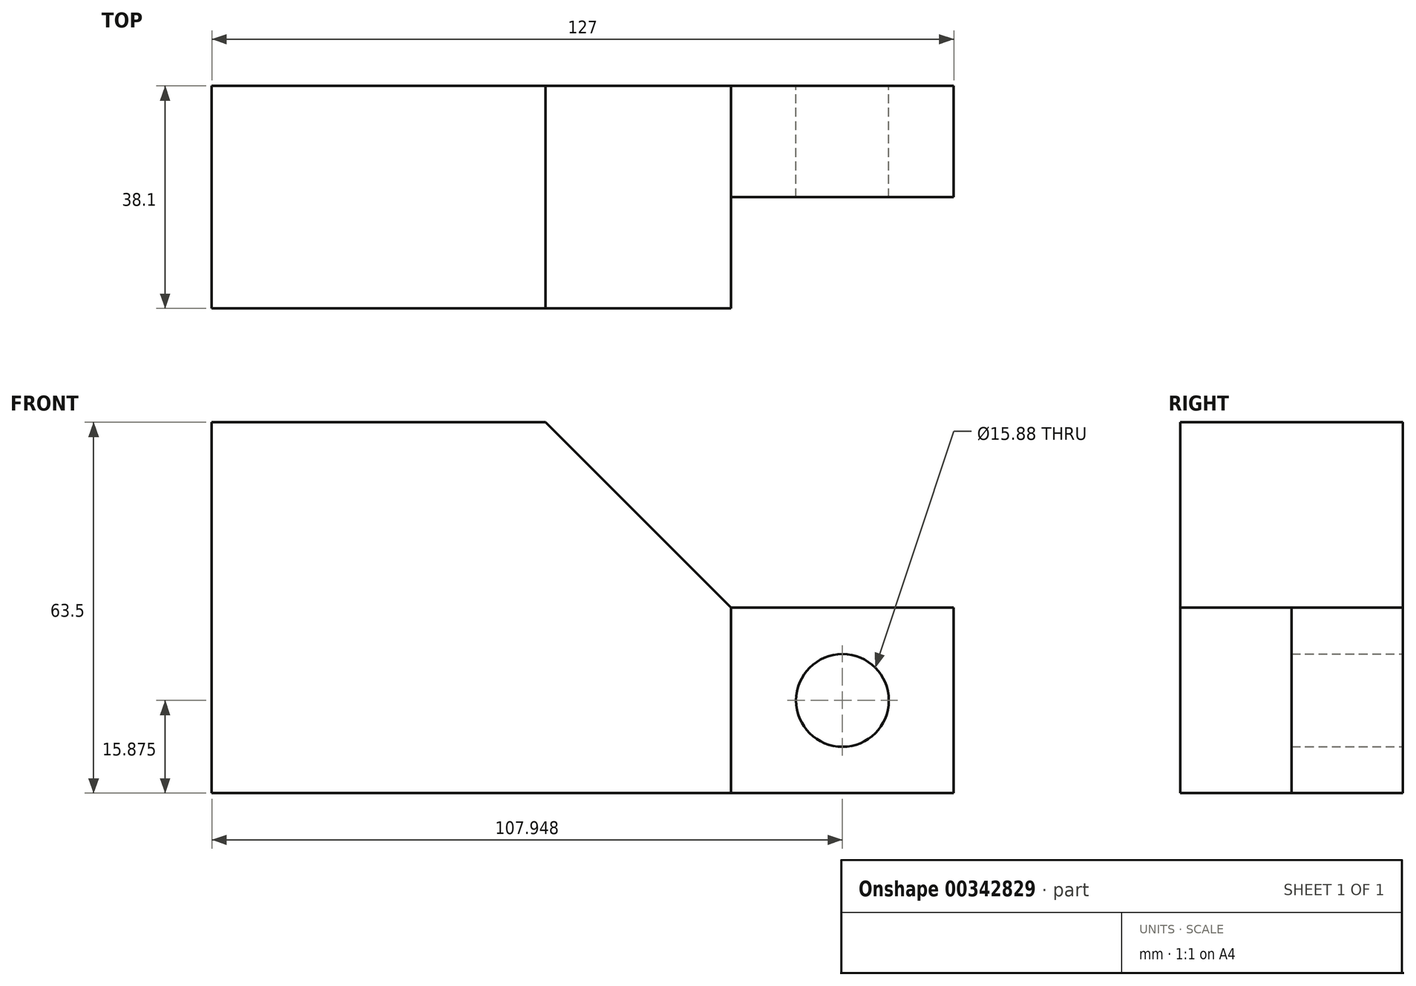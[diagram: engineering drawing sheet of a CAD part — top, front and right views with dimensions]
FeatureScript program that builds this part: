
annotation { "Feature Type Name" : "Feature", "Feature Type Description" : "" }
export const myFeature = defineFeature(function(context is Context, id is Id, definition is map)
    precondition{}
    {
        {
            var Q0;
            Q0=qCreatedBy(makeId("Front.planeOp"),FACE);
            var sketch = newSketch(context, id + "F0", { "sketchPlane" : qUnion([Q0])});
            skLineSegment(sketch, "E0", {"start": v(-13.7, 0) * mm, "end": v(-13.7, -31.75) * mm});
            skLineSegment(sketch, "E1", {"start": v(-13.7, -31.75) * mm, "end": v(24.4, -31.75) * mm});
            skLineSegment(sketch, "E2", {"start": v(24.4, -31.75) * mm, "end": v(24.4, 0) * mm});
            skLineSegment(sketch, "E3", {"start": v(24.4, 0) * mm, "end": v(-13.7, 0) * mm});
            skLineSegment(sketch, "E4", {"start": v(-13.7, -31.75) * mm, "end": v(-102.6, -31.75) * mm});
            skLineSegment(sketch, "E5", {"start": v(-102.6, -31.75) * mm, "end": v(-102.6, 31.75) * mm});
            skCircle(sketch, "E6", {"center": v(5.36, -15.88) * mm, "radius": 7.94 * mm});
            skPoint(sketch, "E6.centerSnap0", {"position": v(5.36, 0) * mm});
            skPoint(sketch, "E6.centerSnap1", {"position": v(24.4, -15.88) * mm});
            skLineSegment(sketch, "E7", {"start": v(-13.7, 0) * mm, "end": v(-45.44, 31.75) * mm});
            skLineSegment(sketch, "E8", {"start": v(-102.6, 31.75) * mm, "end": v(-45.44, 31.75) * mm});
            skSolve(sketch);
        }
        {
            var Q0;
            Q0=makeQuery(id+"F0.imprint","IMPRINT",FACE,{"disambiguationData":[TD([[makeQuery(id+"F0.imprint","IMPRINT",EDGE,{"derivedFrom":sQuery(id+"F0.wireOp",EDGE,"E0")}),-1.0]])]});
            extrude(context, id + "F1", {"entities" : qUnion([Q0]), "depth" : 38.1 * mm});
        }
        {
            var Q0;
            Q0=makeQuery(id+"F0.imprint","IMPRINT",FACE,{"disambiguationData":[TD([[makeQuery(id+"F0.imprint","IMPRINT",EDGE,{"derivedFrom":sQuery(id+"F0.wireOp",EDGE,"E0")}),1.0]])]});
            extrude(context, id + "F2", {"entities" : qUnion([Q0]), "operationType" : NewBodyOperationType.ADD, "depth" : 19.05 * mm});
        }
    });
